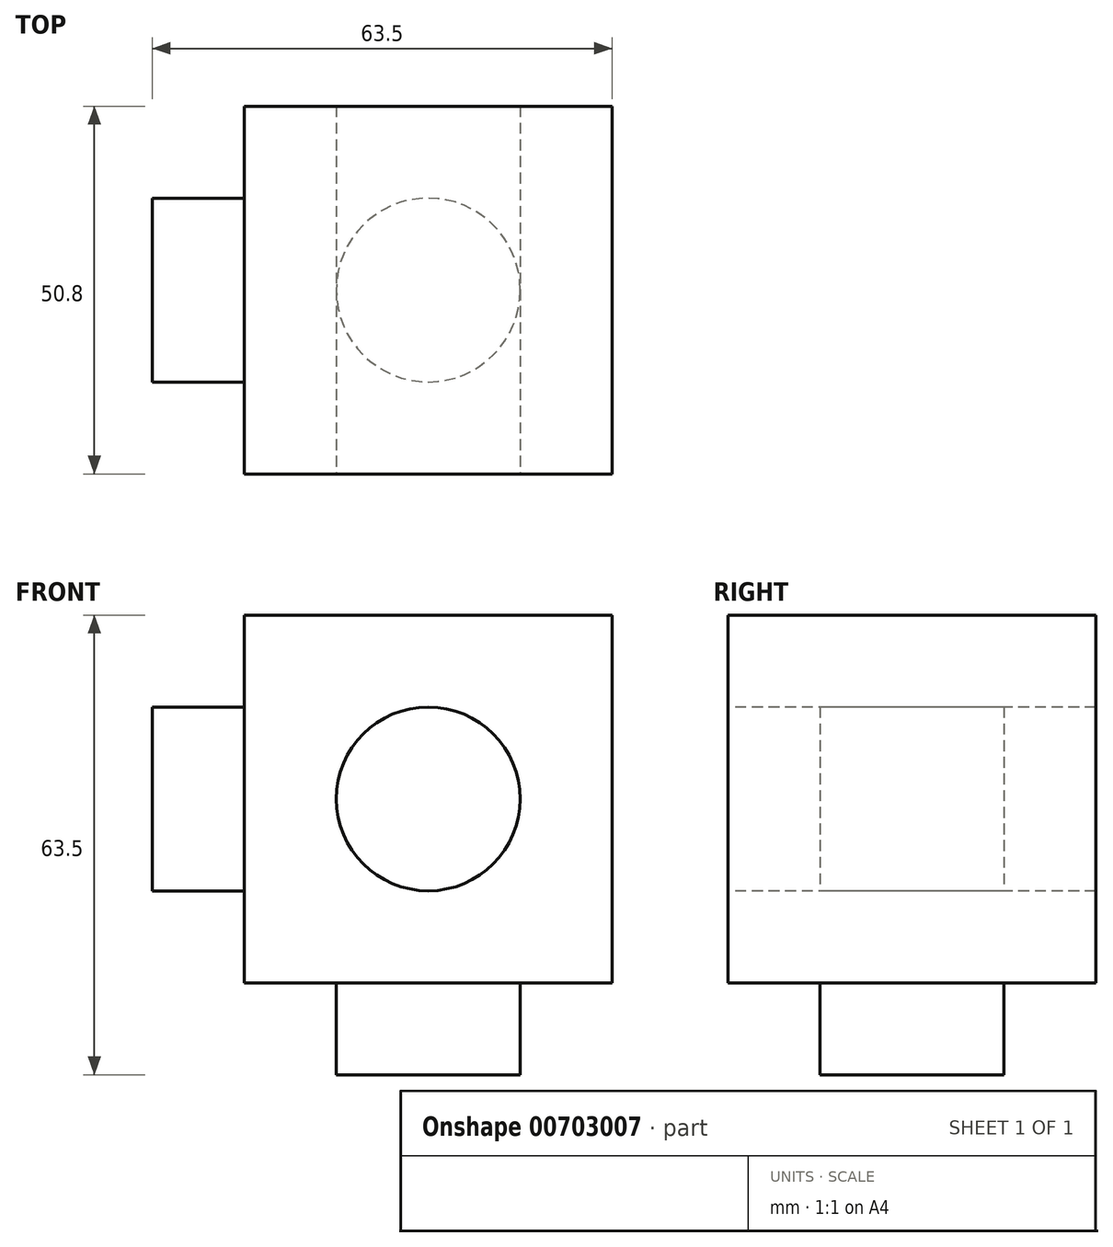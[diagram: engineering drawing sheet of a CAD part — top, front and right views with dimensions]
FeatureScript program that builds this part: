
annotation { "Feature Type Name" : "Feature", "Feature Type Description" : "" }
export const myFeature = defineFeature(function(context is Context, id is Id, definition is map)
    precondition{}
    {
        {
            var Q0;
            Q0=qCreatedBy(makeId("Front.planeOp"),FACE);
            var sketch = newSketch(context, id + "F0", { "sketchPlane" : qUnion([Q0])});
            skLineSegment(sketch, "E0", {"start": v(-18.65, 28.7) * mm, "end": v(-18.65, -22.1) * mm});
            skLineSegment(sketch, "E1", {"start": v(-18.65, -22.1) * mm, "end": v(32.15, -22.1) * mm});
            skLineSegment(sketch, "E2", {"start": v(32.15, -22.1) * mm, "end": v(32.15, 28.7) * mm});
            skLineSegment(sketch, "E3", {"start": v(32.15, 28.7) * mm, "end": v(-18.65, 28.7) * mm});
            skSolve(sketch);
        }
        {
            var Q0;
            Q0 = qSketchRegion(id + "F0", true);
            extrude(context, id + "F1", {"entities" : qUnion([Q0]), "depth" : 50.8 * mm, "offsetDistance" : 25.4 * mm});
        }
        {
            var Q0;
            Q0=makeQuery(id+"F1.opExtrude","CAP_FACE",FACE,{"disambiguationData":[OSD([sQuery(id+"F0.wireOp",EDGE,"E0"),sQuery(id+"F0.wireOp",EDGE,"E1"),sQuery(id+"F0.wireOp",EDGE,"E2"),sQuery(id+"F0.wireOp",EDGE,"E3")])],"isStart":false});
            var sketch = newSketch(context, id + "F2", { "sketchPlane" : qUnion([Q0])});
            skCircle(sketch, "E4", {"center": v(6.75, 3.3) * mm, "radius": 12.7 * mm});
            skSolve(sketch);
        }
        {
            var Q0;
            Q0 = qSketchRegion(id + "F2", true);
            extrude(context, id + "F3", {"entities" : qUnion([Q0]), "operationType" : NewBodyOperationType.REMOVE, "oppositeDirection" : true, "depth" : 50.8 * mm, "offsetDistance" : 25.4 * mm});
        }
        {
            var Q0;
            Q0=makeQuery(id+"F1.opExtrude","SWEPT_FACE",FACE,{"disambiguationData":[OSD([sQuery(id+"F0.wireOp",EDGE,"E1")])]});
            var sketch = newSketch(context, id + "F4", { "sketchPlane" : qUnion([Q0])});
            skCircle(sketch, "E5", {"center": v(6.75, 25.4) * mm, "radius": 12.7 * mm});
            skSolve(sketch);
        }
        {
            var Q0;
            Q0 = qSketchRegion(id + "F4", true);
            extrude(context, id + "F5", {"entities" : qUnion([Q0]), "operationType" : NewBodyOperationType.ADD, "depth" : 12.7 * mm, "offsetDistance" : 25.4 * mm});
        }
        {
            var Q0;
            Q0=makeQuery(id+"F1.opExtrude","SWEPT_FACE",FACE,{"disambiguationData":[OSD([sQuery(id+"F0.wireOp",EDGE,"E0")])]});
            var sketch = newSketch(context, id + "F6", { "sketchPlane" : qUnion([Q0])});
            skLineSegment(sketch, "E6.bottom", {"start": v(12.7, 16) * mm, "end": v(38.1, 16) * mm});
            skLineSegment(sketch, "E6.top", {"start": v(12.7, -9.4) * mm, "end": v(38.1, -9.4) * mm});
            skLineSegment(sketch, "E6.left", {"start": v(12.7, 16) * mm, "end": v(12.7, -9.4) * mm});
            skLineSegment(sketch, "E6.right", {"start": v(38.1, 16) * mm, "end": v(38.1, -9.4) * mm});
            skSolve(sketch);
        }
        {
            var Q0;
            Q0 = qSketchRegion(id + "F6", true);
            extrude(context, id + "F7", {"entities" : qUnion([Q0]), "operationType" : NewBodyOperationType.ADD, "depth" : 12.7 * mm, "offsetDistance" : 25.4 * mm});
        }
    });
